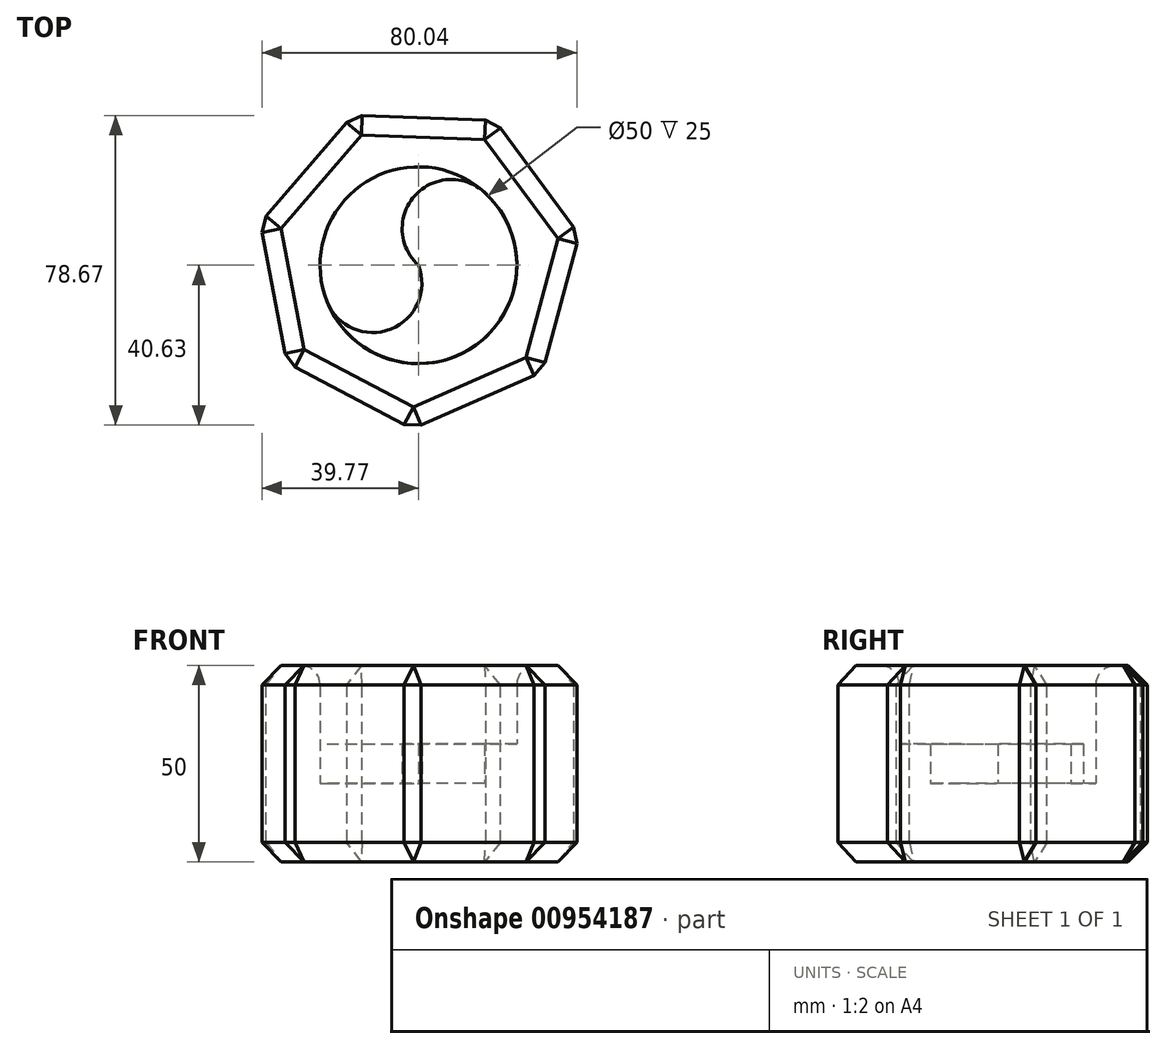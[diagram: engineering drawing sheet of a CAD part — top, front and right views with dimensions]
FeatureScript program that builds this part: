
annotation { "Feature Type Name" : "Feature", "Feature Type Description" : "" }
export const myFeature = defineFeature(function(context is Context, id is Id, definition is map)
    precondition{}
    {
        {
            var Q0;
            Q0=qCreatedBy(makeId("Top.planeOp"),FACE);
            var sketch = newSketch(context, id + "F0", { "sketchPlane" : qUnion([Q0])});
            skCircle(sketch, "E0.cCircle", {"center": v(0, 0) * mm, "radius": 37.5 * mm, "construction": true});
            skLineSegment(sketch, "E0.0", {"start": v(40.89, 7.8) * mm, "end": v(31.59, -27.1) * mm});
            skLineSegment(sketch, "E0.1", {"start": v(31.59, -27.1) * mm, "end": v(-1.5, -41.6) * mm});
            skLineSegment(sketch, "E0.2", {"start": v(-1.5, -41.6) * mm, "end": v(-33.45, -24.76) * mm});
            skLineSegment(sketch, "E0.3", {"start": v(-33.45, -24.76) * mm, "end": v(-40.22, 10.72) * mm});
            skLineSegment(sketch, "E0.4", {"start": v(-40.22, 10.72) * mm, "end": v(-16.7, 38.13) * mm});
            skLineSegment(sketch, "E0.5", {"start": v(-16.7, 38.13) * mm, "end": v(19.4, 36.83) * mm});
            skLineSegment(sketch, "E0.6", {"start": v(19.4, 36.83) * mm, "end": v(40.89, 7.8) * mm});
            skPoint(sketch, "E0.0.midPoint", {"position": v(36.24, -9.66) * mm});
            skCircle(sketch, "E1", {"center": v(0, 0) * mm, "radius": 25 * mm});
            skArc(sketch, "E2", {"start": v(-23.24, -9.22) * mm, "mid": v(-7, -16.23) * mm, "end": v(0, 0) * mm});
            skArc(sketch, "E3", {"start": v(16.74, 18.57) * mm, "mid": v(-0.91, 17.65) * mm, "end": v(0, 0) * mm});
            skSolve(sketch);
        }
        {
            var Q0;
            Q0=makeQuery(id+"F0.imprint","IMPRINT",FACE,{"disambiguationData":[TD([[makeQuery(id+"F0.imprint","IMPRINT",EDGE,{"derivedFrom":sQuery(id+"F0.wireOp",EDGE,"E0.0")}),-1.0]])]});
            extrude(context, id + "F1", {"entities" : qUnion([Q0]), "depth" : 50 * mm, "offsetDistance" : 25 * mm});
        }
        {
            var Q0;
            {var subQ0=sQuery(id+"F0.wireOp",EDGE,"E2");Q0=makeQuery(id+"F0.imprint","IMPRINT",FACE,{"disambiguationData":[TD([[makeQuery(id+"F0.imprint","IMPRINT",EDGE,{"derivedFrom":subQ0}),1.0]])]});}
            extrude(context, id + "F2", {"entities" : qUnion([Q0]), "operationType" : NewBodyOperationType.ADD, "depth" : 20 * mm, "offsetDistance" : 25 * mm});
        }
        {
            var Q0;
            {var subQ0=sQuery(id+"F0.wireOp",EDGE,"E2");Q0=makeQuery(id+"F0.imprint","IMPRINT",FACE,{"disambiguationData":[TD([[makeQuery(id+"F0.imprint","IMPRINT",EDGE,{"derivedFrom":subQ0}),-1.0]])]});}
            extrude(context, id + "F3", {"entities" : qUnion([Q0]), "operationType" : NewBodyOperationType.ADD, "depth" : 30 * mm, "offsetDistance" : 25 * mm});
        }
        {
            var Q0;
            Q0=makeQuery(id+"F1.opExtrude","CAP_EDGE",EDGE,{"disambiguationData":[OSD([sQuery(id+"F0.wireOp",EDGE,"E1")])],"isStart":false});
            fillet(context, id + "F4", {"entities" : qUnion([Q0]), "radius" : 5 * mm, "tangentPropagation" : true, "allowEdgeOverflow" : false});
        }
        {
            var Q0;
            Q0=makeQuery(id+"F1.opExtrude","CAP_EDGE",EDGE,{"disambiguationData":[OSD([sQuery(id+"F0.wireOp",EDGE,"E0.3")])],"isStart":false});
            var Q1;
            Q1=makeQuery(id+"F1.opExtrude","CAP_EDGE",EDGE,{"disambiguationData":[OSD([sQuery(id+"F0.wireOp",EDGE,"E0.4")])],"isStart":false});
            var Q2;
            Q2=makeQuery(id+"F1.opExtrude","CAP_EDGE",EDGE,{"disambiguationData":[OSD([sQuery(id+"F0.wireOp",EDGE,"E0.5")])],"isStart":false});
            var Q3;
            Q3=makeQuery(id+"F1.opExtrude","CAP_EDGE",EDGE,{"disambiguationData":[OSD([sQuery(id+"F0.wireOp",EDGE,"E0.6")])],"isStart":false});
            var Q4;
            Q4=makeQuery(id+"F1.opExtrude","CAP_EDGE",EDGE,{"disambiguationData":[OSD([sQuery(id+"F0.wireOp",EDGE,"E0.0")])],"isStart":false});
            var Q5;
            Q5=makeQuery(id+"F1.opExtrude","CAP_EDGE",EDGE,{"disambiguationData":[OSD([sQuery(id+"F0.wireOp",EDGE,"E0.1")])],"isStart":false});
            var Q6;
            Q6=makeQuery(id+"F1.opExtrude","CAP_EDGE",EDGE,{"disambiguationData":[OSD([sQuery(id+"F0.wireOp",EDGE,"E0.2")])],"isStart":false});
            var Q7;
            Q7=makeQuery(id+"F1.opExtrude","CAP_EDGE",EDGE,{"disambiguationData":[OSD([sQuery(id+"F0.wireOp",EDGE,"E0.4")])],"isStart":true});
            var Q8;
            Q8=makeQuery(id+"F1.opExtrude","CAP_EDGE",EDGE,{"disambiguationData":[OSD([sQuery(id+"F0.wireOp",EDGE,"E0.3")])],"isStart":true});
            var Q9;
            Q9=makeQuery(id+"F1.opExtrude","CAP_EDGE",EDGE,{"disambiguationData":[OSD([sQuery(id+"F0.wireOp",EDGE,"E0.2")])],"isStart":true});
            var Q10;
            Q10=makeQuery(id+"F1.opExtrude","CAP_EDGE",EDGE,{"disambiguationData":[OSD([sQuery(id+"F0.wireOp",EDGE,"E0.1")])],"isStart":true});
            var Q11;
            Q11=makeQuery(id+"F1.opExtrude","CAP_EDGE",EDGE,{"disambiguationData":[OSD([sQuery(id+"F0.wireOp",EDGE,"E0.0")])],"isStart":true});
            var Q12;
            Q12=makeQuery(id+"F1.opExtrude","CAP_EDGE",EDGE,{"disambiguationData":[OSD([sQuery(id+"F0.wireOp",EDGE,"E0.6")])],"isStart":true});
            var Q13;
            Q13=makeQuery(id+"F1.opExtrude","CAP_EDGE",EDGE,{"disambiguationData":[OSD([sQuery(id+"F0.wireOp",EDGE,"E0.5")])],"isStart":true});
            var Q14;
            Q14=makeQuery(id+"F1.opExtrude","SWEPT_EDGE",EDGE,{"disambiguationData":[OSD([sQuery(id+"F0.wireOp",EDGE,"E0.0"),sQuery(id+"F0.wireOp",EDGE,"E0.6")])]});
            var Q15;
            Q15=makeQuery(id+"F1.opExtrude","SWEPT_EDGE",EDGE,{"disambiguationData":[OSD([sQuery(id+"F0.wireOp",EDGE,"E0.5"),sQuery(id+"F0.wireOp",EDGE,"E0.6")])]});
            var Q16;
            Q16=makeQuery(id+"F1.opExtrude","SWEPT_EDGE",EDGE,{"disambiguationData":[OSD([sQuery(id+"F0.wireOp",EDGE,"E0.4"),sQuery(id+"F0.wireOp",EDGE,"E0.5")])]});
            var Q17;
            Q17=makeQuery(id+"F1.opExtrude","SWEPT_EDGE",EDGE,{"disambiguationData":[OSD([sQuery(id+"F0.wireOp",EDGE,"E0.3"),sQuery(id+"F0.wireOp",EDGE,"E0.4")])]});
            var Q18;
            Q18=makeQuery(id+"F1.opExtrude","SWEPT_EDGE",EDGE,{"disambiguationData":[OSD([sQuery(id+"F0.wireOp",EDGE,"E0.2"),sQuery(id+"F0.wireOp",EDGE,"E0.3")])]});
            var Q19;
            Q19=makeQuery(id+"F1.opExtrude","SWEPT_EDGE",EDGE,{"disambiguationData":[OSD([sQuery(id+"F0.wireOp",EDGE,"E0.1"),sQuery(id+"F0.wireOp",EDGE,"E0.2")])]});
            var Q20;
            Q20=makeQuery(id+"F1.opExtrude","SWEPT_EDGE",EDGE,{"disambiguationData":[OSD([sQuery(id+"F0.wireOp",EDGE,"E0.0"),sQuery(id+"F0.wireOp",EDGE,"E0.1")])]});
            chamfer(context, id + "F5", {"entities" : qUnion([Q0, Q1, Q2, Q3, Q4, Q5, Q6, Q7, Q8, Q9, Q10, Q11, Q12, Q13, Q14, Q15, Q16, Q17, Q18, Q19, Q20]), "width" : 5 * mm, "tangentPropagation" : true});
        }
    });
